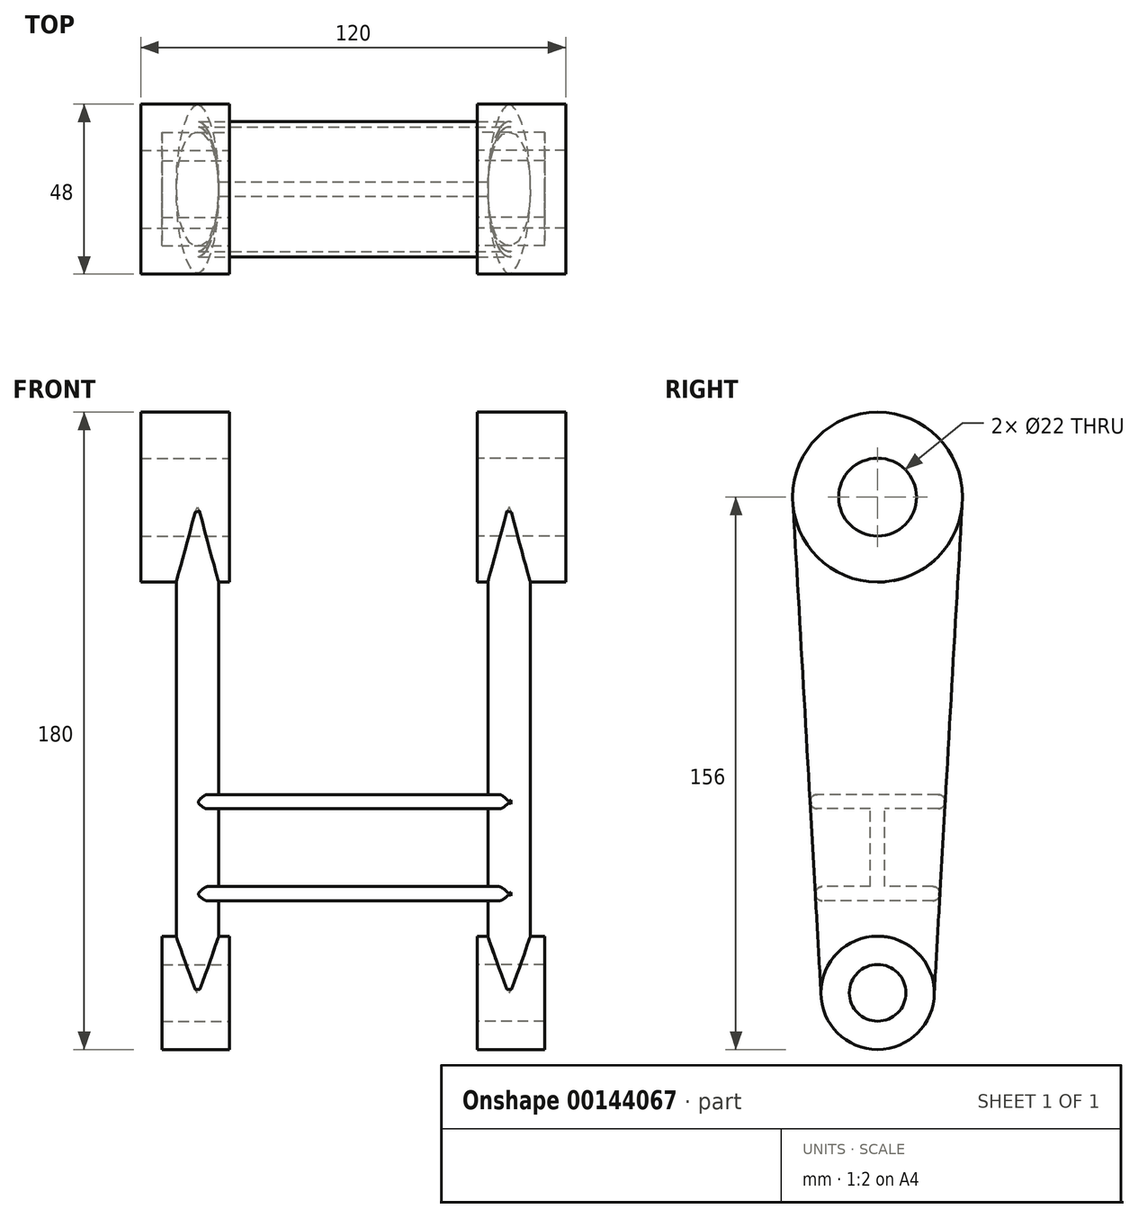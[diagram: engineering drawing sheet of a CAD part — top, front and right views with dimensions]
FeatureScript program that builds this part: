
annotation { "Feature Type Name" : "Feature", "Feature Type Description" : "" }
export const myFeature = defineFeature(function(context is Context, id is Id, definition is map)
    precondition{}
    {
        {
            var Q0;
            Q0=qCreatedBy(makeId("Right.planeOp"),FACE);
            var sketch = newSketch(context, id + "F0", { "sketchPlane" : qUnion([Q0])});
            skCircle(sketch, "E0", {"center": v(0, 0) * mm, "radius": 8 * mm});
            skCircle(sketch, "E1", {"center": v(0, 0) * mm, "radius": 16 * mm});
            skCircle(sketch, "E2", {"center": v(0, 140) * mm, "radius": 11 * mm});
            skCircle(sketch, "E3", {"center": v(0, 140) * mm, "radius": 24 * mm});
            skSolve(sketch);
        }
        {
            var Q0;
            Q0=makeQuery(id+"F0.imprint","IMPRINT",FACE,{"disambiguationData":[TD([[makeQuery(id+"F0.imprint","IMPRINT",EDGE,{"derivedFrom":sQuery(id+"F0.wireOp",EDGE,"E2")}),-1.0]])]});
            var Q1;
            Q1=makeQuery(id+"F0.imprint","IMPRINT",FACE,{"disambiguationData":[TD([[makeQuery(id+"F0.imprint","IMPRINT",EDGE,{"derivedFrom":sQuery(id+"F0.wireOp",EDGE,"E2")}),1.0]])]});
            extrude(context, id + "F1", {"entities" : qUnion([Q0, Q1]), "depth" : 25 * mm});
        }
        {
            var Q0;
            Q0=makeQuery(id+"F0.imprint","IMPRINT",FACE,{"disambiguationData":[TD([[makeQuery(id+"F0.imprint","IMPRINT",EDGE,{"derivedFrom":sQuery(id+"F0.wireOp",EDGE,"E0")}),1.0]])]});
            var Q1;
            Q1=makeQuery(id+"F0.imprint","IMPRINT",FACE,{"disambiguationData":[TD([[makeQuery(id+"F0.imprint","IMPRINT",EDGE,{"derivedFrom":sQuery(id+"F0.wireOp",EDGE,"E0")}),-1.0]])]});
            var Q2;
            Q2=sQuery(id+"F0.wireOp",EDGE,"E1");
            extrude(context, id + "F2", {"entities" : qUnion([Q0, Q1]), "surfaceEntities" : qUnion([Q2]), "depth" : 19 * mm});
        }
        {
            var Q0;
            Q0=qCreatedBy(makeId("Top.planeOp"),FACE);
            var sketch = newSketch(context, id + "F3", { "sketchPlane" : qUnion([Q0])});
            skLineSegment(sketch, "E4", {"start": v(0, 16) * mm, "end": v(18, 16) * mm, "construction": true});
            skEllipse(sketch, "E5", {"center": v(9, 0) * mm, "majorRadius": 16 * mm, "minorRadius": 6 * mm, "majorAxis": v(0, 1)});
            skPoint(sketch, "E5.centerSnap0", {"position": v(9, 16) * mm});
            skPoint(sketch, "E6", {"position": v(3, 0) * mm});
            skSolve(sketch);
        }
        {
            var Q0;
            Q0=sQuery(id+"F0.wireOp",VERTEX,"E3.center");
            var Q1;
            Q1=qCreatedBy(makeId("Top.planeOp"),FACE);
            cPlane(context, id + "F4", {"entities" : qUnion([Q0, Q1]), "cplaneType" : CPlaneType.PLANE_POINT, "offset" : 25 * mm, "width" : 150 * mm, "height" : 150 * mm});
        }
        {
            var Q0;
            Q0=qCreatedBy(id+"F4.planeOp",FACE);
            var sketch = newSketch(context, id + "F5", { "sketchPlane" : qUnion([Q0])});
            skEllipse(sketch, "E7.0", {"center": v(9, 0) * mm, "majorRadius": 24 * mm, "minorRadius": 6 * mm, "majorAxis": v(0, 1)});
            skLineSegment(sketch, "E8", {"start": v(0, 24) * mm, "end": v(25, 24) * mm, "construction": true});
            skLineSegment(sketch, "E9", {"start": v(25, -24) * mm, "end": v(0, -24) * mm, "construction": true});
            skPoint(sketch, "E10", {"position": v(3, 0) * mm});
            skLineSegment(sketch, "E11", {"start": v(0, 0) * mm, "end": v(25.09, 0) * mm, "construction": true});
            skPoint(sketch, "E11.endSnap0", {"position": v(15, 0) * mm});
            skSolve(sketch);
        }
        {
            var Q0;
            Q0=makeQuery(id+"F5.imprint","IMPRINT",FACE,{"disambiguationData":[TD([[makeQuery(id+"F5.imprint","IMPRINT",EDGE,{"derivedFrom":sQuery(id+"F5.wireOp",EDGE,"E7.0")}),1.0]])]});
            var Q1;
            Q1=makeQuery(id+"F3.imprint","IMPRINT",FACE,{"disambiguationData":[TD([[makeQuery(id+"F3.imprint","IMPRINT",EDGE,{"derivedFrom":sQuery(id+"F3.wireOp",EDGE,"E5")}),1.0]])]});
            loft(context, id + "F6", {"operationType" : NewBodyOperationType.ADD, "sheetProfilesArray" : [{ "sheetProfileEntities" : qUnion([Q0]) }, { "sheetProfileEntities" : qUnion([Q1]) }]});
        }
        {
            var Q0;
            Q0=makeQuery(id+"F0.imprint","IMPRINT",FACE,{"disambiguationData":[TD([[makeQuery(id+"F0.imprint","IMPRINT",EDGE,{"derivedFrom":sQuery(id+"F0.wireOp",EDGE,"E2")}),1.0]])]});
            var Q1;
            Q1=makeQuery(id+"F0.imprint","IMPRINT",FACE,{"disambiguationData":[TD([[makeQuery(id+"F0.imprint","IMPRINT",EDGE,{"derivedFrom":sQuery(id+"F0.wireOp",EDGE,"E0")}),1.0]])]});
            extrude(context, id + "F7", {"entities" : qUnion([Q0, Q1]), "operationType" : NewBodyOperationType.REMOVE, "endBound" : BoundingType.THROUGH_ALL, "depth" : 25 * mm});
        }
        {
            var Q0;
            Q0=qCreatedBy(makeId("Right.planeOp"),FACE);
            cPlane(context, id + "F8", {"entities" : qUnion([Q0]), "cplaneType" : CPlaneType.OFFSET, "offset" : (70 / 2) * mm, "oppositeDirection" : true, "width" : 150 * mm, "height" : 150 * mm});
        }
        {
            var Q0;
            Q0=makeQuery(id+"F1.opExtrude","SWEPT_BODY",BODY,{"disambiguationData":[OSD([sQuery(id+"F0.wireOp",EDGE,"E3")])]});
            var Q1;
            Q1=qCreatedBy(id+"F8.planeOp",FACE);
            mirror(context, id + "F9", {"entities" : qUnion([Q0]), "mirrorPlane" : qUnion([Q1])});
        }
        {
            var Q0;
            Q0=qCreatedBy(makeId("Right.planeOp"),FACE);
            cPlane(context, id + "F10", {"entities" : qUnion([Q0]), "cplaneType" : CPlaneType.OFFSET, "offset" : 9.5 * mm, "width" : 150 * mm, "height" : 150 * mm});
        }
        {
            var Q0;
            Q0=qCreatedBy(id+"F10.planeOp",FACE);
            var sketch = newSketch(context, id + "F11", { "sketchPlane" : qUnion([Q0])});
            skLineSegment(sketch, "E12", {"start": v(23.96, 138.62) * mm, "end": v(16, 0) * mm, "construction": true});
            skLineSegment(sketch, "E13", {"start": v(-23.97, 138.85) * mm, "end": v(-16, 0) * mm, "construction": true});
            skSolve(sketch);
        }
        {
            var Q0;
            Q0=qCreatedBy(id+"F10.planeOp",FACE);
            var sketch = newSketch(context, id + "F12", { "sketchPlane" : qUnion([Q0])});
            skLineSegment(sketch, "E14", {"start": v(-15.6, 26) * mm, "end": v(15.6, 26) * mm});
            skLineSegment(sketch, "E15", {"start": v(-17.1, 56) * mm, "end": v(17.1, 56) * mm});
            skLineSegment(sketch, "E16", {"start": v(-17.1, 52) * mm, "end": v(-2, 52) * mm});
            skArc(sketch, "E17", {"start": v(-17.1, 56) * mm, "mid": v(-19.1, 54) * mm, "end": v(-17.1, 52) * mm});
            skArc(sketch, "E18", {"start": v(17.1, 52) * mm, "mid": v(19.1, 54) * mm, "end": v(17.1, 56) * mm});
            skLineSegment(sketch, "E19", {"start": v(-15.6, 30) * mm, "end": v(-2, 30) * mm});
            skArc(sketch, "E20", {"start": v(15.6, 26) * mm, "mid": v(17.6, 28) * mm, "end": v(15.6, 30) * mm});
            skArc(sketch, "E21", {"start": v(-15.6, 30) * mm, "mid": v(-17.6, 28) * mm, "end": v(-15.6, 26) * mm});
            skLineSegment(sketch, "E22", {"start": v(-2, 52) * mm, "end": v(-2, 30) * mm});
            skLineSegment(sketch, "E23", {"start": v(2, 52) * mm, "end": v(2, 30) * mm});
            skLineSegment(sketch, "E24.trimOffspring", {"start": v(2, 52) * mm, "end": v(17.1, 52) * mm});
            skLineSegment(sketch, "E25.trimOffspring", {"start": v(2, 30) * mm, "end": v(15.6, 30) * mm});
            skPoint(sketch, "E26.orphan", {"position": v(0, 52) * mm});
            skPoint(sketch, "E27", {"position": v(-19.1, 54) * mm});
            skPoint(sketch, "E28", {"position": v(19.1, 54) * mm});
            skPoint(sketch, "E29", {"position": v(17.6, 28) * mm});
            skPoint(sketch, "E30", {"position": v(-17.6, 28) * mm});
            skLineSegment(sketch, "E31.0", {"start": v(23.96, 138.62) * mm, "end": v(16, 0) * mm, "construction": true});
            skSolve(sketch);
        }
        {
            var Q0;
            Q0=makeQuery(id+"F12.imprint","IMPRINT",FACE,{"disambiguationData":[TD([[makeQuery(id+"F12.imprint","IMPRINT",EDGE,{"derivedFrom":sQuery(id+"F12.wireOp",EDGE,"E14")}),1.0]])]});
            var Q1;
            Q1=makeQuery(id+"F9.opPattern","COPY",FACE,{"derivedFrom":makeQuery(id+"F2.opExtrude","CAP_FACE",FACE,{"disambiguationData":[OSD([sQuery(id+"F0.wireOp",EDGE,"E1")])],"isStart":false}),"instanceName":"1"});
            extrude(context, id + "F13", {"entities" : qUnion([Q0]), "operationType" : NewBodyOperationType.ADD, "oppositeDirection" : true, "endBoundEntityFace" : qUnion([Q1]), "depth" : 88.28 * mm});
        }
    });
